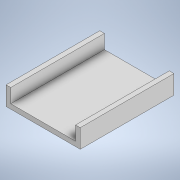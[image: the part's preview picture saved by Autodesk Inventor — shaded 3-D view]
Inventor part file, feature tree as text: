
AUTODESK INVENTOR PART (.ipt)
format: ipt  version: 2021 (Build 250183000, 183)  size: 98,816 bytes
history: native  units: in
note: dims shown in document units (in); Inventor stores cm internally (conversion verified against a paired STEP export)
features: extrude x1, sketch x1
ambient origin geometry x8: Origin, YZ Plane, XZ Plane, XY Plane, X Axis, Y Axis, Z Axis, Center Point
bodies: Solid1 (feature_tree)
feature tree (2):
  extrude  "Extrusion1"  Depth=0.5in
  sketch  "Sketch1"  dims[d2=1.98in d3=0.5in d4=0.5in d5=0.125in d6=2.5in d7=0.0in]
